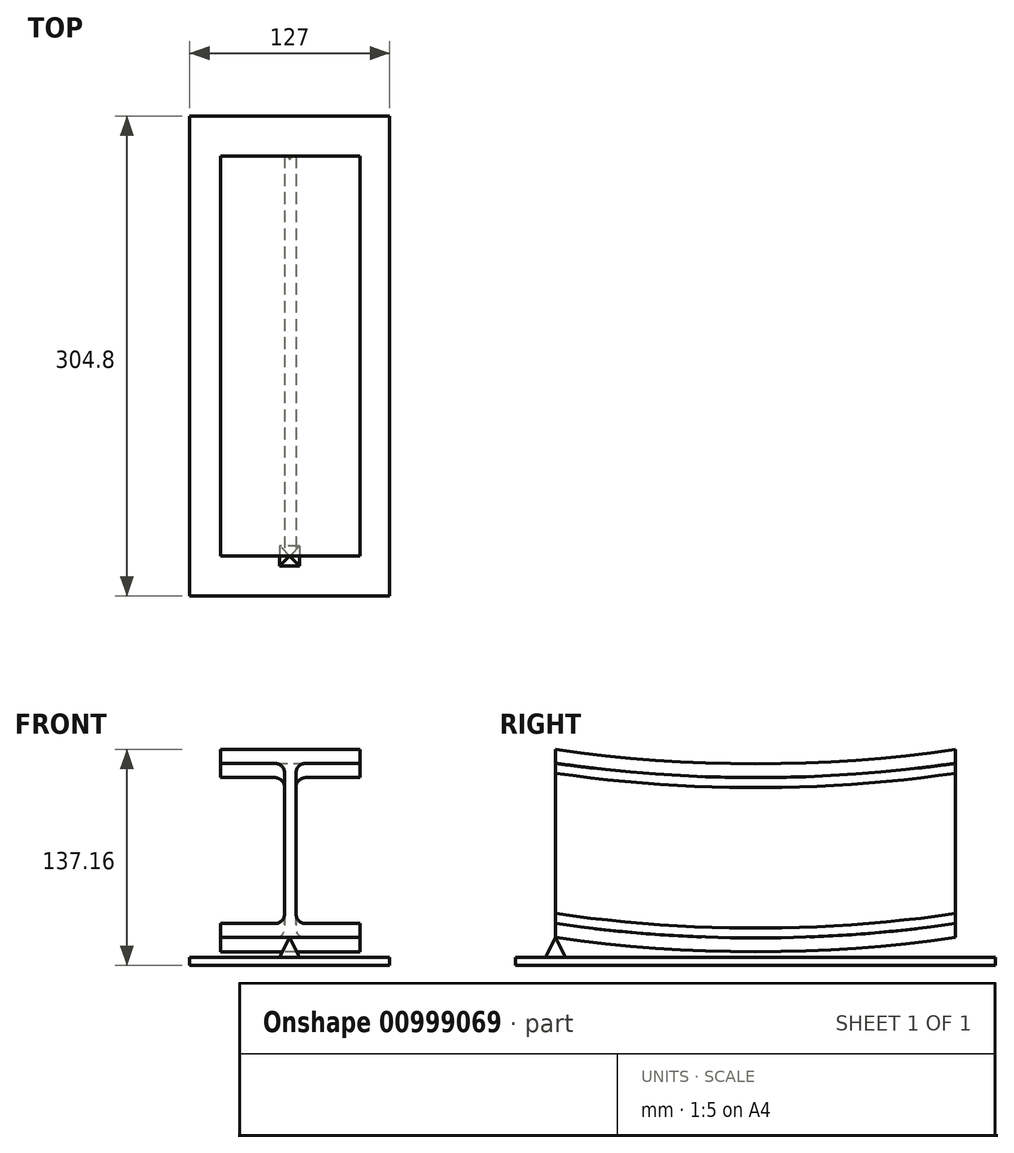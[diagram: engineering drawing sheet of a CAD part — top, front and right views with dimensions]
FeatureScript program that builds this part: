
annotation { "Feature Type Name" : "Feature", "Feature Type Description" : "" }
export const myFeature = defineFeature(function(context is Context, id is Id, definition is map)
    precondition{}
    {
        {
            var Q0;
            Q0=qCreatedBy(makeId("Front.planeOp"),FACE);
            var sketch = newSketch(context, id + "F0", { "sketchPlane" : qUnion([Q0])});
            skLineSegment(sketch, "E0.top", {"start": v(-3.1, 50.93) * mm, "end": v(-3.26, 50.93) * mm});
            skLineSegment(sketch, "E0.left", {"start": v(3.85, -44.58) * mm, "end": v(3.85, 44.58) * mm});
            skLineSegment(sketch, "E0.right", {"start": v(-3.26, -44.58) * mm, "end": v(-3.26, 44.58) * mm});
            skPoint(sketch, "E0.middle", {"position": v(0, 0) * mm});
            skLineSegment(sketch, "E1.bottom", {"start": v(-43.9, 59.69) * mm, "end": v(44.5, 59.7) * mm});
            skLineSegment(sketch, "E1.top", {"start": v(-43.9, 50.93) * mm, "end": v(-9.6, 50.93) * mm});
            skLineSegment(sketch, "E1.left", {"start": v(-43.9, 59.69) * mm, "end": v(-43.9, 50.93) * mm});
            skLineSegment(sketch, "E1.right", {"start": v(44.5, 59.7) * mm, "end": v(44.5, 50.93) * mm});
            skLineSegment(sketch, "E2.bottom", {"start": v(-43.9, -50.93) * mm, "end": v(-9.6, -50.93) * mm});
            skLineSegment(sketch, "E2.top", {"start": v(-43.9, -59.7) * mm, "end": v(44.5, -59.69) * mm});
            skLineSegment(sketch, "E2.left", {"start": v(-43.9, -50.93) * mm, "end": v(-43.9, -59.7) * mm});
            skLineSegment(sketch, "E2.right", {"start": v(44.5, -50.93) * mm, "end": v(44.5, -59.69) * mm});
            skPoint(sketch, "E3.newPointA", {"position": v(42.94, 50.93) * mm});
            skArc(sketch, "E3.filletArc", {"start": v(-3.26, 44.58) * mm, "mid": v(-5.12, 49.07) * mm, "end": v(-9.6, 50.93) * mm});
            skLineSegment(sketch, "E4", {"start": v(44.5, 50.93) * mm, "end": v(10.2, 50.93) * mm});
            skPoint(sketch, "E5.newPointA", {"position": v(3.85, 37.04) * mm});
            skArc(sketch, "E5.filletArc", {"start": v(10.2, 50.93) * mm, "mid": v(5.71, 49.07) * mm, "end": v(3.85, 44.58) * mm});
            skArc(sketch, "E6.filletArc", {"start": v(-9.6, -50.93) * mm, "mid": v(-5.12, -49.07) * mm, "end": v(-3.26, -44.58) * mm});
            skLineSegment(sketch, "E7", {"start": v(10.2, -50.93) * mm, "end": v(44.5, -50.93) * mm});
            skArc(sketch, "E8.filletArc", {"start": v(3.85, -44.58) * mm, "mid": v(5.71, -49.07) * mm, "end": v(10.2, -50.93) * mm});
            skSolve(sketch);
        }
        {
            var Q0;
            Q0=qCreatedBy(makeId("Front.planeOp"),FACE);
            cPlane(context, id + "F1", {"entities" : qUnion([Q0]), "cplaneType" : CPlaneType.OFFSET, "offset" : 254 * mm, "width" : 152.4 * mm, "height" : 152.4 * mm});
        }
        {
            var Q0;
            Q0=qCreatedBy(id+"F1.planeOp",FACE);
            var sketch = newSketch(context, id + "F2", { "sketchPlane" : qUnion([Q0])});
            skLineSegment(sketch, "E9.top", {"start": v(-5.51, 50.93) * mm, "end": v(-5.68, 50.93) * mm});
            skLineSegment(sketch, "E9.left", {"start": v(3.85, -44.58) * mm, "end": v(3.85, 44.58) * mm});
            skLineSegment(sketch, "E9.right", {"start": v(-3.26, -44.58) * mm, "end": v(-3.26, 44.58) * mm});
            skPoint(sketch, "E9.middle", {"position": v(-2.42, 0) * mm});
            skLineSegment(sketch, "E10.bottom", {"start": v(-43.9, 59.69) * mm, "end": v(44.5, 59.7) * mm});
            skLineSegment(sketch, "E10.top", {"start": v(-43.9, 50.93) * mm, "end": v(-9.6, 50.93) * mm});
            skLineSegment(sketch, "E10.left", {"start": v(-43.9, 59.69) * mm, "end": v(-43.9, 50.93) * mm});
            skLineSegment(sketch, "E10.right", {"start": v(44.5, 59.7) * mm, "end": v(44.5, 50.93) * mm});
            skLineSegment(sketch, "E11.bottom", {"start": v(-43.9, -50.93) * mm, "end": v(-9.6, -50.93) * mm});
            skLineSegment(sketch, "E11.top", {"start": v(-43.9, -59.7) * mm, "end": v(44.5, -59.69) * mm});
            skLineSegment(sketch, "E11.left", {"start": v(-43.9, -50.93) * mm, "end": v(-43.9, -59.7) * mm});
            skLineSegment(sketch, "E11.right", {"start": v(44.5, -50.93) * mm, "end": v(44.5, -59.69) * mm});
            skPoint(sketch, "E12.newPointA", {"position": v(40.52, 50.93) * mm});
            skArc(sketch, "E12.filletArc", {"start": v(-3.26, 44.58) * mm, "mid": v(-5.12, 49.07) * mm, "end": v(-9.6, 50.93) * mm});
            skLineSegment(sketch, "E13", {"start": v(44.5, 50.93) * mm, "end": v(10.2, 50.93) * mm});
            skPoint(sketch, "E14.newPointA", {"position": v(3.85, 37.04) * mm});
            skArc(sketch, "E14.filletArc", {"start": v(10.2, 50.93) * mm, "mid": v(5.71, 49.07) * mm, "end": v(3.85, 44.58) * mm});
            skArc(sketch, "E15.filletArc", {"start": v(-9.6, -50.93) * mm, "mid": v(-5.12, -49.07) * mm, "end": v(-3.26, -44.58) * mm});
            skLineSegment(sketch, "E16", {"start": v(10.2, -50.93) * mm, "end": v(44.5, -50.93) * mm});
            skArc(sketch, "E17.filletArc", {"start": v(3.85, -44.58) * mm, "mid": v(5.71, -49.07) * mm, "end": v(10.2, -50.93) * mm});
            skSolve(sketch);
        }
        {
            var Q0;
            Q0=qCreatedBy(makeId("Right.planeOp"),FACE);
            var sketch = newSketch(context, id + "F3", { "sketchPlane" : qUnion([Q0])});
            skArc(sketch, "E18", {"start": v(-253.97, 0) * mm, "mid": v(-126.99, -9.11) * mm, "end": v(0, 0) * mm});
            skSolve(sketch);
        }
        {
            var Q0;
            Q0=qCreatedBy(id+"F1.planeOp",FACE);
            var sketch = newSketch(context, id + "F4", { "sketchPlane" : qUnion([Q0])});
            skLineSegment(sketch, "E19.bottom", {"start": v(6.35, -59.7) * mm, "end": v(-6.35, -59.7) * mm});
            skLineSegment(sketch, "E19.top", {"start": v(6.35, -72.4) * mm, "end": v(-6.35, -72.4) * mm});
            skLineSegment(sketch, "E19.left", {"start": v(6.35, -59.7) * mm, "end": v(6.35, -72.4) * mm});
            skLineSegment(sketch, "E19.right", {"start": v(-6.35, -59.7) * mm, "end": v(-6.35, -72.4) * mm});
            skPoint(sketch, "E19.middle", {"position": v(0, -66.04) * mm});
            skSolve(sketch);
        }
        {
            var Q0;
            Q0=makeQuery(id+"F4.imprint","IMPRINT",FACE,{"disambiguationData":[TD([[makeQuery(id+"F4.imprint","IMPRINT",EDGE,{"derivedFrom":sQuery(id+"F4.wireOp",EDGE,"E19.bottom")}),1.0]])]});
            extrude(context, id + "F5", {"entities" : qUnion([Q0]), "endBound" : BoundingType.SYMMETRIC, "oppositeDirection" : true, "depth" : 12.7 * mm, "offsetDistance" : 25.4 * mm});
        }
        {
            var Q0;
            Q0=makeQuery(id+"F5.opExtrude","SWEPT_FACE",FACE,{"disambiguationData":[OSD([sQuery(id+"F4.wireOp",EDGE,"E19.left")])]});
            var sketch = newSketch(context, id + "F6", { "sketchPlane" : qUnion([Q0])});
            skLineSegment(sketch, "E20", {"start": v(-254, -59.69) * mm, "end": v(-260.35, -72.39) * mm});
            skLineSegment(sketch, "E21", {"start": v(-260.35, -72.4) * mm, "end": v(-260.35, -59.7) * mm});
            skLineSegment(sketch, "E22", {"start": v(-260.35, -59.7) * mm, "end": v(-254, -59.69) * mm});
            skLineSegment(sketch, "E23", {"start": v(-254, -59.69) * mm, "end": v(-247.65, -72.4) * mm});
            skLineSegment(sketch, "E24", {"start": v(-247.65, -72.4) * mm, "end": v(-247.65, -59.7) * mm});
            skLineSegment(sketch, "E25", {"start": v(-247.65, -59.7) * mm, "end": v(-254, -59.69) * mm});
            skSolve(sketch);
        }
        {
            var Q0;
            Q0=makeQuery(id+"F6.imprint","IMPRINT",FACE,{"disambiguationData":[TD([[makeQuery(id+"F6.imprint","IMPRINT",EDGE,{"derivedFrom":sQuery(id+"F6.wireOp",EDGE,"E20")}),-1.0]])]});
            var Q1;
            Q1=makeQuery(id+"F6.imprint","IMPRINT",FACE,{"disambiguationData":[TD([[makeQuery(id+"F6.imprint","IMPRINT",EDGE,{"derivedFrom":sQuery(id+"F6.wireOp",EDGE,"E23")}),1.0]])]});
            extrude(context, id + "F7", {"entities" : qUnion([Q0, Q1]), "operationType" : NewBodyOperationType.REMOVE, "endBound" : BoundingType.THROUGH_ALL, "oppositeDirection" : true, "depth" : 25.4 * mm, "offsetDistance" : 25.4 * mm});
        }
        {
            var Q0;
            Q0=qCreatedBy(id+"F1.planeOp",FACE);
            var sketch = newSketch(context, id + "F8", { "sketchPlane" : qUnion([Q0])});
            skLineSegment(sketch, "E26", {"start": v(0, -59.69) * mm, "end": v(-6.35, -72.39) * mm});
            skLineSegment(sketch, "E27", {"start": v(-6.35, -72.39) * mm, "end": v(-6.35, -59.69) * mm});
            skLineSegment(sketch, "E28", {"start": v(-6.35, -59.69) * mm, "end": v(0, -59.69) * mm});
            skSolve(sketch);
        }
        {
            var Q0;
            Q0 = qSketchRegion(id + "F8", true);
            extrude(context, id + "F9", {"entities" : qUnion([Q0]), "operationType" : NewBodyOperationType.REMOVE, "endBound" : BoundingType.SYMMETRIC, "oppositeDirection" : true, "depth" : 25.4 * mm, "offsetDistance" : 25.4 * mm});
        }
        {
            var Q0;
            Q0=qCreatedBy(id+"F1.planeOp",FACE);
            var sketch = newSketch(context, id + "F10", { "sketchPlane" : qUnion([Q0])});
            skLineSegment(sketch, "E29", {"start": v(0, -59.69) * mm, "end": v(6.35, -72.39) * mm});
            skLineSegment(sketch, "E30", {"start": v(6.35, -72.39) * mm, "end": v(6.35, -59.69) * mm});
            skLineSegment(sketch, "E31", {"start": v(6.35, -59.69) * mm, "end": v(0, -59.69) * mm});
            skSolve(sketch);
        }
        {
            var Q0;
            Q0 = qSketchRegion(id + "F10", true);
            extrude(context, id + "F11", {"entities" : qUnion([Q0]), "operationType" : NewBodyOperationType.REMOVE, "endBound" : BoundingType.SYMMETRIC, "depth" : 25.4 * mm, "offsetDistance" : 25.4 * mm});
        }
        {
            var Q0;
            Q0=makeQuery(id+"F5.opExtrude","SWEPT_FACE",FACE,{"disambiguationData":[OSD([sQuery(id+"F4.wireOp",EDGE,"E19.top")])]});
            cPlane(context, id + "F12", {"entities" : qUnion([Q0]), "cplaneType" : CPlaneType.OFFSET, "offset" : 0 * mm, "width" : 152.4 * mm, "height" : 152.4 * mm});
        }
        {
            var Q0;
            Q0=qCreatedBy(id+"F12.planeOp",FACE);
            var sketch = newSketch(context, id + "F13", { "sketchPlane" : qUnion([Q0])});
            skLineSegment(sketch, "E32.bottom", {"start": v(-63.5, 279.4) * mm, "end": v(63.5, 279.4) * mm});
            skLineSegment(sketch, "E32.top", {"start": v(-63.5, -25.4) * mm, "end": v(63.5, -25.4) * mm});
            skLineSegment(sketch, "E32.left", {"start": v(-63.5, 279.4) * mm, "end": v(-63.5, -25.4) * mm});
            skLineSegment(sketch, "E32.right", {"start": v(63.5, 279.4) * mm, "end": v(63.5, -25.4) * mm});
            skSolve(sketch);
        }
        {
            var Q0;
            Q0=makeQuery(id+"F13.imprint","IMPRINT",FACE,{"disambiguationData":[TD([[makeQuery(id+"F13.imprint","IMPRINT",EDGE,{"derivedFrom":sQuery(id+"F13.wireOp",EDGE,"E32.bottom")}),-1.0]])]});
            extrude(context, id + "F14", {"entities" : qUnion([Q0]), "operationType" : NewBodyOperationType.ADD, "depth" : 5.08 * mm, "offsetDistance" : 25.4 * mm});
        }
        {
            var Q0;
            Q0=qCreatedBy(makeId("Front.planeOp"),FACE);
            var sketch = newSketch(context, id + "F15", { "sketchPlane" : qUnion([Q0])});
            skLineSegment(sketch, "E33", {"start": v(0, -59.7) * mm, "end": v(0, -72.4) * mm});
            skArc(sketch, "E34", {"start": v(0, -59.7) * mm, "mid": v(-6.35, -66.04) * mm, "end": v(0, -72.4) * mm});
            skSolve(sketch);
        }
        {
            var Q0;
            Q0=makeQuery(id+"F15.imprint","IMPRINT",FACE,{"disambiguationData":[TD([[makeQuery(id+"F15.imprint","IMPRINT",EDGE,{"derivedFrom":sQuery(id+"F15.wireOp",EDGE,"E33")}),-1.0]])]});
            var Q1;
            Q1=sQuery(id+"F15.wireOp",EDGE,"E33");
            revolve(context, id + "F16", {"surfaceOperationType" : NewSurfaceOperationType.NEW, "entities" : qUnion([Q0]), "axis" : qUnion([Q1]), "revolveType" : RevolveType.FULL});
        }
        {
            var Q0;
            Q0=makeQuery(id+"F0.imprint","IMPRINT",FACE,{"disambiguationData":[TD([[makeQuery(id+"F0.imprint","IMPRINT",EDGE,{"derivedFrom":sQuery(id+"F0.wireOp",EDGE,"E0.left")}),1.0]])]});
            var Q1;
            Q1=makeQuery(id+"F2.imprint","IMPRINT",FACE,{"disambiguationData":[TD([[makeQuery(id+"F2.imprint","IMPRINT",EDGE,{"derivedFrom":sQuery(id+"F2.wireOp",EDGE,"E9.left")}),1.0]])]});
            var Q2;
            Q2=sQuery(id+"F3.wireOp",EDGE,"E18");
            sweep(context, id + "F17", {"operationType" : NewBodyOperationType.ADD, "profiles" : qUnion([Q0, Q1]), "path" : qUnion([Q2]), "keepProfileOrientation" : true});
        }
    });
